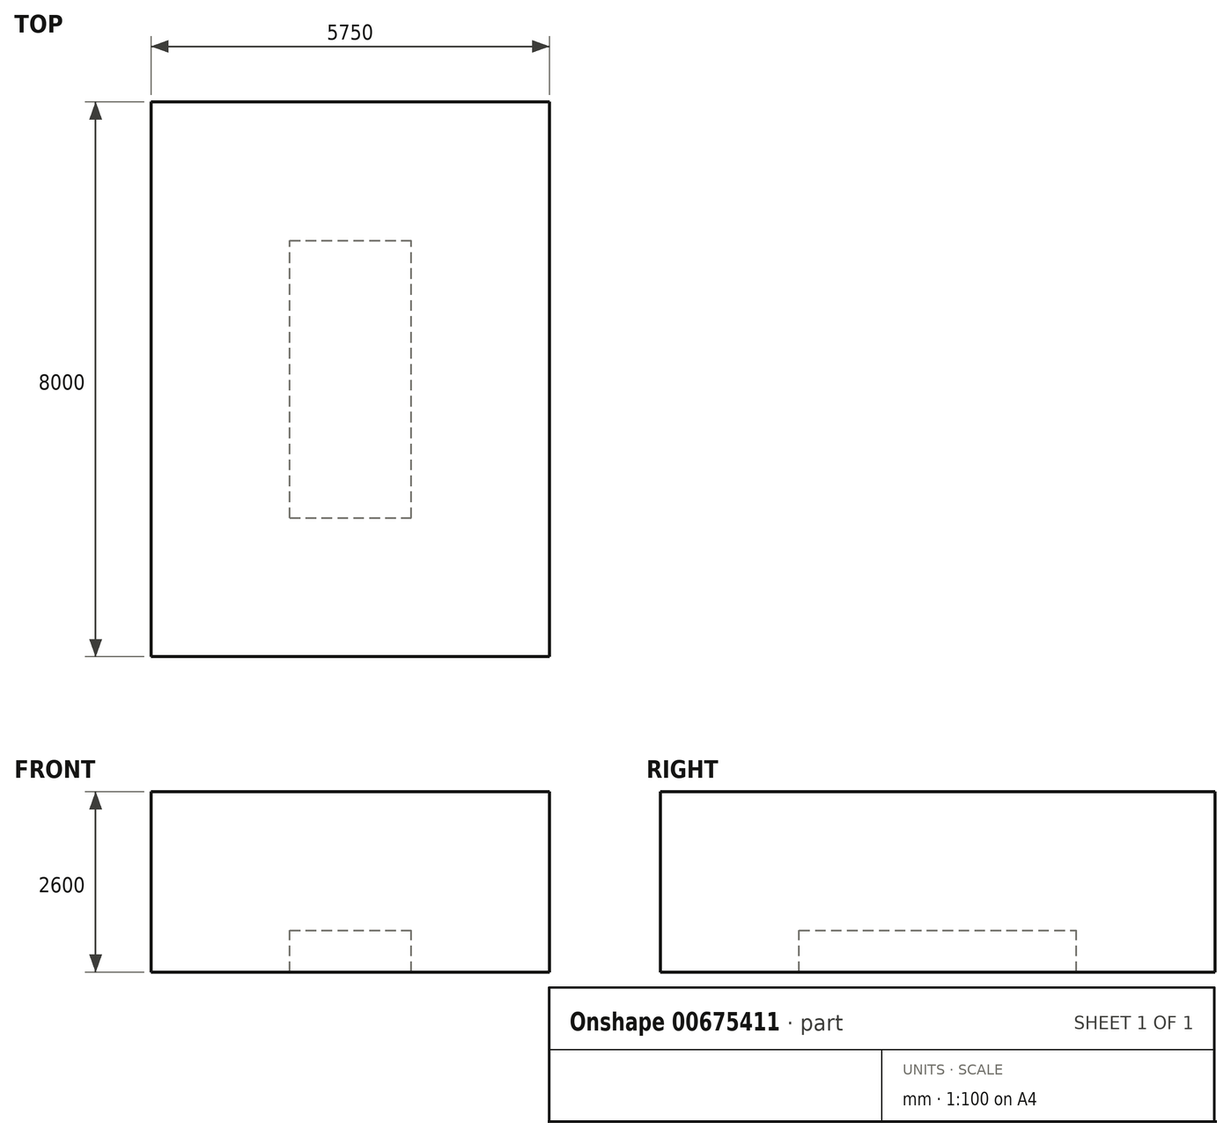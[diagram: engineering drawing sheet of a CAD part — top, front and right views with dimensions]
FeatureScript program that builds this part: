
annotation { "Feature Type Name" : "Feature", "Feature Type Description" : "" }
export const myFeature = defineFeature(function(context is Context, id is Id, definition is map)
    precondition{}
    {
        {
            var Q0;
            Q0=qCreatedBy(makeId("Front.planeOp"),FACE);
            var sketch = newSketch(context, id + "F0", { "sketchPlane" : qUnion([Q0])});
            skLineSegment(sketch, "E0.bottom", {"start": v(0, 0) * mm, "end": v(1750, 0) * mm});
            skLineSegment(sketch, "E0.top", {"start": v(0, 600) * mm, "end": v(1750, 600) * mm});
            skLineSegment(sketch, "E0.left", {"start": v(0, 0) * mm, "end": v(0, 600) * mm});
            skLineSegment(sketch, "E0.right", {"start": v(1750, 0) * mm, "end": v(1750, 600) * mm});
            skSolve(sketch);
        }
        {
            var Q0;
            Q0=qSketchRegion(id+"F0",true);
            extrude(context, id + "F1", {"entities" : qUnion([Q0]), "depth" : 4000 * mm, "offsetDistance" : 25 * mm});
        }
        {
            var Q0;
            Q0=qCreatedBy(makeId("Top.planeOp"),FACE);
            var sketch = newSketch(context, id + "F2", { "sketchPlane" : qUnion([Q0])});
            skLineSegment(sketch, "E1.bottom", {"start": v(-2000, 2000) * mm, "end": v(3750, 2000) * mm});
            skLineSegment(sketch, "E1.top", {"start": v(-2000, -6000) * mm, "end": v(3750, -6000) * mm});
            skLineSegment(sketch, "E1.left", {"start": v(-2000, 2000) * mm, "end": v(-2000, -6000) * mm});
            skLineSegment(sketch, "E1.right", {"start": v(3750, 2000) * mm, "end": v(3750, -6000) * mm});
            skSolve(sketch);
        }
        {
            var Q0;
            Q0=qSketchRegion(id+"F2",true);
            extrude(context, id + "F3", {"entities" : qUnion([Q0]), "depth" : 2600 * mm, "offsetDistance" : 25 * mm});
        }
        {
            var Q0;
            Q0=makeQuery(id+"F1.opExtrude","SWEPT_BODY",BODY,{"disambiguationData":[OSD([sQuery(id+"F0.wireOp",EDGE,"E0.bottom"),sQuery(id+"F0.wireOp",EDGE,"E0.top"),sQuery(id+"F0.wireOp",EDGE,"E0.left"),sQuery(id+"F0.wireOp",EDGE,"E0.right")])]});
            var Q1;
            Q1=makeQuery(id+"F3.opExtrude","SWEPT_BODY",BODY,{"disambiguationData":[OSD([sQuery(id+"F2.wireOp",EDGE,"E1.bottom"),sQuery(id+"F2.wireOp",EDGE,"E1.top"),sQuery(id+"F2.wireOp",EDGE,"E1.left"),sQuery(id+"F2.wireOp",EDGE,"E1.right")])]});
            booleanBodies(context, id + "F4", {"operationType" : BooleanOperationType.SUBTRACTION, "tools" : qUnion([Q0]), "targets" : qUnion([Q1])});
        }
        {
            var Q0;
            Q0=makeQuery(id+"F3.opExtrude","CAP_FACE",FACE,{"disambiguationData":[OSD([sQuery(id+"F2.wireOp",EDGE,"E1.bottom"),sQuery(id+"F2.wireOp",EDGE,"E1.top"),sQuery(id+"F2.wireOp",EDGE,"E1.left"),sQuery(id+"F2.wireOp",EDGE,"E1.right")])],"isStart":true});
            var sketch = newSketch(context, id + "F5", { "sketchPlane" : qUnion([Q0])});
            skLineSegment(sketch, "E2.bottom", {"start": v(0, 4000) * mm, "end": v(1750, 4000) * mm});
            skLineSegment(sketch, "E2.top", {"start": v(0, 0) * mm, "end": v(1750, 0) * mm});
            skLineSegment(sketch, "E2.left", {"start": v(0, 4000) * mm, "end": v(0, 0) * mm});
            skLineSegment(sketch, "E2.right", {"start": v(1750, 4000) * mm, "end": v(1750, 0) * mm});
            skSolve(sketch);
        }
        {
            var Q0;
            Q0 = qSketchRegion(id + "F5", true);
            var Q1;
            Q1=makeQuery(id+"F4.opBoolean","COPY",FACE,{"derivedFrom":makeQuery(id+"F1.opExtrude","SWEPT_FACE",FACE,{"disambiguationData":[OSD([sQuery(id+"F0.wireOp",EDGE,"E0.top")])]})});
            extrude(context, id + "F6", {"entities" : qUnion([Q0]), "endBound" : BoundingType.UP_TO_SURFACE, "oppositeDirection" : true, "depth" : 25 * mm, "endBoundEntityFace" : qUnion([Q1]), "offsetDistance" : 25 * mm});
        }
    });
